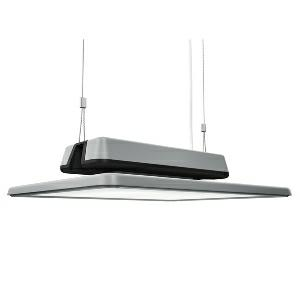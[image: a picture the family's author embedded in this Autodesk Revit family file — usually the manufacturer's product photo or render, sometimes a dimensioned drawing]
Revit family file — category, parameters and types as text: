
# Revit family: acaneo_-_hial_20000_850_w_dali_00734228_9ae8
name_source: partatom
category: Lighting Fixtures
units: mm (PartAtom-declared; Revit-internal decimal feet)

## family parameters
Cut with Voids When Loaded = No
Host = Face
Light Source = No
Part Type = Normal
Room Calculation Point = No
Round Connector Dimension = Use Diameter
Shared = No

## types (1)
- ACANEO - HIAL 20000/850/W/DALI (1 x LED, 22000 lm, 5000K)
    Apparent Load = 140 VA
    Approval mark = CE
    CIE Flux Codes = 76 97 99 100 100
    Color Rendering = 80-89
    Color Temperature = 5000K
    Control Gear = Electronic ballast
    Default Elevation = 1800 mm
    Description = HIAL 20000/850/W/DALI|High bay luminaire|light source: LED|work equipment: Adjustable electronic ballast, digital DALI|connected load: 220-240 V, 50/60 Hz|Power consumption: approx. 140 W|power factor: approx. 0,951|luminous flux: 22000 lm|luminous efficacy: 157 lm/W|colour temperature: Cold white, ca. 5000 K|color rendering index (CRI): >= 80|chromaticity tolerance:  3 SDCM|System of protection: IP 65|class of protection: I|technology: Continuously dimmable|luminaire body|material: Aluminium|surface: Powder coatet|colour: White aluminium|lamp cover: Acrylic (PMMA), Clear|weight (net): approx. 8.2 kg|mains lead: Built-in plug RST 20i5 Einbau|Fastening: Available separately|Accessory: Junction box (RST 20i5)|minimum ambient temperature: -30 ░C|maximum ambient temperature: 70 ░C|glare control: Optics|unified glare rating(4H 8H): <=  25|
    Frequency = 50 Hz, 60 Hz
    Height = 125 mm
    Lamp = 1 x LED
    Lamp Light Flux = 22000 lm
    Lamp count = 1
    Length = 480 mm
    Luminous efficacy = 157 lm/W
    Manufacturer = Waldmann
    ModVariant = No
    Model = 00734228
    Mounting Place = Ceiling
    Mounting Type = Pendant
    Number of Poles = 1
    OnlyDefault = Yes
    Power Factor = 1
    Product Name = ACANEO - HIAL 20000/850/W/DALI
    Product group = High bay luminaire (industry)
    ProductGroupID = 901
    Protection Class = Protection class I
    Protection Degree = IP 65
    RLX_Detail_Level = 1
    RLX_Emergency_Light_Flux = 0 lm
    RLX_Emergency_Type = 0
    RLX_Emergency_Type_DB = No
    RlxData = <blob elided: 31309 chars, md5=13ef47ac>
    Socket = socket
    Standby Power = 0 W
    System Light Flux = 22000 lm
    System Power = 140 W
    Type Comments = Product without accessories
    Type Image = acaneo-hial.jpg
    URL = http://relux.com
    VarID = ---
    Voltage = 230 V
    Voltage Range = 110-120 V, 220-240 V
    Weight = 0.00 kg
    Width = 405 mm

## geometry (parser evidence)
native form markers: Blend x4, Sweep x9
no freeform markers — native parametric forms only
